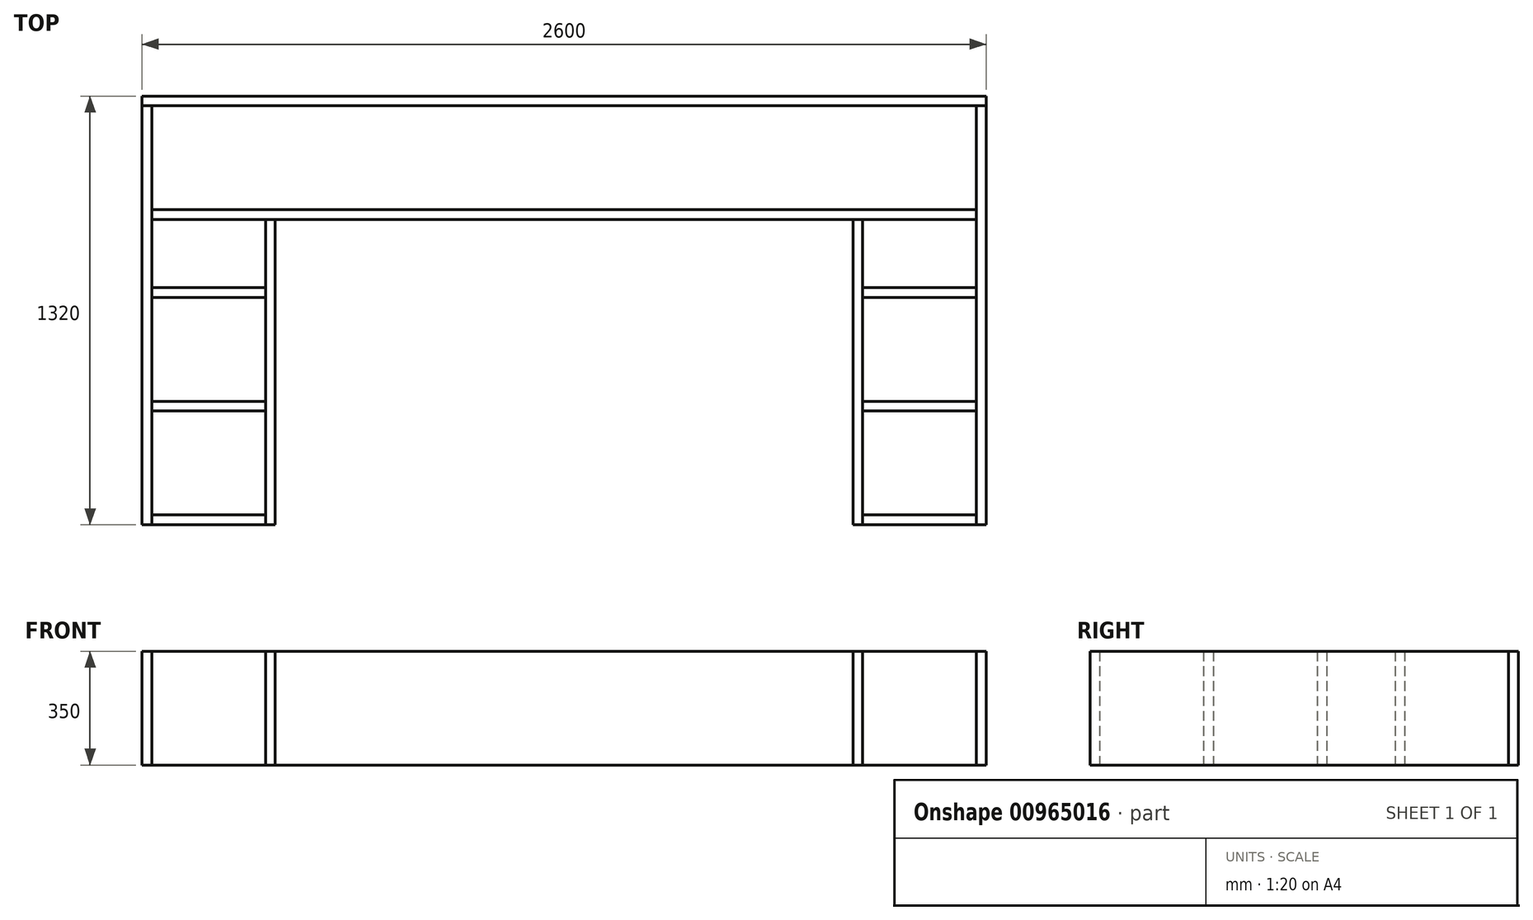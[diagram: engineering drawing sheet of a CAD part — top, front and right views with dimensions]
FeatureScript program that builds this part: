
annotation { "Feature Type Name" : "Feature", "Feature Type Description" : "" }
export const myFeature = defineFeature(function(context is Context, id is Id, definition is map)
    precondition{}
    {
        {
            var Q0;
            Q0=qCreatedBy(makeId("Top.planeOp"),FACE);
            var sketch = newSketch(context, id + "F0", { "sketchPlane" : qUnion([Q0])});
            skLineSegment(sketch, "E0.bottom", {"start": v(1300, 1125) * mm, "end": v(-1300, 1125) * mm});
            skLineSegment(sketch, "E0.top", {"start": v(1300, -1125) * mm, "end": v(-1300, -1125) * mm});
            skLineSegment(sketch, "E0.left", {"start": v(1300, 1125) * mm, "end": v(1300, -1125) * mm});
            skLineSegment(sketch, "E0.right", {"start": v(-1300, 1125) * mm, "end": v(-1300, -1125) * mm});
            skPoint(sketch, "E0.middle", {"position": v(0, 0) * mm});
            skLineSegment(sketch, "E1", {"start": v(-1300, -195) * mm, "end": v(1300, -195) * mm});
            skLineSegment(sketch, "E2", {"start": v(-1300, 1095) * mm, "end": v(1300, 1095) * mm});
            skLineSegment(sketch, "E3", {"start": v(-1270, 1095) * mm, "end": v(-1270, -195) * mm});
            skLineSegment(sketch, "E4", {"start": v(1270, 1095) * mm, "end": v(1270, -195) * mm});
            skLineSegment(sketch, "E5", {"start": v(-1270, 775) * mm, "end": v(1270, 775) * mm});
            skLineSegment(sketch, "E6", {"start": v(-1270, 745) * mm, "end": v(1270, 745) * mm});
            skLineSegment(sketch, "E7", {"start": v(-920, 745) * mm, "end": v(-920, -195) * mm});
            skLineSegment(sketch, "E8", {"start": v(-890, 745) * mm, "end": v(-890, -195) * mm});
            skLineSegment(sketch, "E9", {"start": v(920, 745) * mm, "end": v(920, -195) * mm});
            skLineSegment(sketch, "E10", {"start": v(890, 745) * mm, "end": v(890, -195) * mm});
            skLineSegment(sketch, "E11", {"start": v(-1270, 155) * mm, "end": v(-920, 155) * mm});
            skPoint(sketch, "E11.endSnap0", {"position": v(-920, 275) * mm});
            skLineSegment(sketch, "E12", {"start": v(-1270, 185) * mm, "end": v(-920, 185) * mm});
            skLineSegment(sketch, "E13", {"start": v(-1270, -165) * mm, "end": v(-920, -165) * mm});
            skLineSegment(sketch, "E14", {"start": v(-1270, 505) * mm, "end": v(-920, 505) * mm});
            skLineSegment(sketch, "E15", {"start": v(-1270, 535) * mm, "end": v(-920, 535) * mm});
            skLineSegment(sketch, "E16", {"start": v(920, 155) * mm, "end": v(1270, 155) * mm});
            skLineSegment(sketch, "E17", {"start": v(920, -165) * mm, "end": v(1270, -165) * mm});
            skLineSegment(sketch, "E18", {"start": v(920, 185) * mm, "end": v(1270, 185) * mm});
            skLineSegment(sketch, "E19", {"start": v(920, 505) * mm, "end": v(1270, 505) * mm});
            skLineSegment(sketch, "E20", {"start": v(920, 535) * mm, "end": v(1270, 535) * mm});
            skSolve(sketch);
        }
        {
            var Q0;
            {var subQ5=sQuery(id+"F0.wireOp",EDGE,"E13");Q0=makeQuery(id+"F0.imprint","IMPRINT",FACE,{"disambiguationData":[TD([[makeQuery(id+"F0.imprint","IMPRINT",EDGE,{"derivedFrom":subQ5}),-1.0]])]});}
            var Q1;
            {var subQ0=sQuery(id+"F0.wireOp",EDGE,"E11");Q1=makeQuery(id+"F0.imprint","IMPRINT",FACE,{"disambiguationData":[TD([[makeQuery(id+"F0.imprint","IMPRINT",EDGE,{"derivedFrom":subQ0}),1.0]])]});}
            var Q2;
            {var subQ0=sQuery(id+"F0.wireOp",EDGE,"E14");Q2=makeQuery(id+"F0.imprint","IMPRINT",FACE,{"disambiguationData":[TD([[makeQuery(id+"F0.imprint","IMPRINT",EDGE,{"derivedFrom":subQ0}),1.0]])]});}
            var Q3;
            {var subQ4=sQuery(id+"F0.wireOp",EDGE,"E5");Q3=makeQuery(id+"F0.imprint","IMPRINT",FACE,{"disambiguationData":[TD([[makeQuery(id+"F0.imprint","IMPRINT",EDGE,{"derivedFrom":subQ4}),-1.0]])]});}
            var Q4;
            {var subQ1=sQuery(id+"F0.wireOp",EDGE,"E0.bottom");Q4=makeQuery(id+"F0.imprint","IMPRINT",FACE,{"disambiguationData":[TD([[makeQuery(id+"F0.imprint","IMPRINT",EDGE,{"derivedFrom":subQ1}),1.0]])]});}
            var Q5;
            {var subQ0=sQuery(id+"F0.wireOp",EDGE,"E19");Q5=makeQuery(id+"F0.imprint","IMPRINT",FACE,{"disambiguationData":[TD([[makeQuery(id+"F0.imprint","IMPRINT",EDGE,{"derivedFrom":subQ0}),1.0]])]});}
            var Q6;
            {var subQ0=sQuery(id+"F0.wireOp",EDGE,"E16");Q6=makeQuery(id+"F0.imprint","IMPRINT",FACE,{"disambiguationData":[TD([[makeQuery(id+"F0.imprint","IMPRINT",EDGE,{"derivedFrom":subQ0}),1.0]])]});}
            var Q7;
            {var subQ5=sQuery(id+"F0.wireOp",EDGE,"E17");Q7=makeQuery(id+"F0.imprint","IMPRINT",FACE,{"disambiguationData":[TD([[makeQuery(id+"F0.imprint","IMPRINT",EDGE,{"derivedFrom":subQ5}),-1.0]])]});}
            extrude(context, id + "F1", {"entities" : qUnion([Q0, Q1, Q2, Q3, Q4, Q5, Q6, Q7]), "depth" : 350 * mm, "offsetDistance" : 25 * mm});
        }
        {
            var Q0;
            {var subQ7=sQuery(id+"F0.wireOp",EDGE,"E1");var subQ8=sQuery(id+"F0.wireOp",EDGE,"E0.right");var subQ9=makeQuery(id+"F0.imprint","INTERSECT",VERTEX,{"derivedFrom":[subQ8,subQ7]});Q0=makeQuery(id+"F0.imprint","IMPRINT",FACE,{"disambiguationData":[TD([[makeQuery(id+"F0.imprint","IMPRINT",EDGE,{"disambiguationData":[TD([[subQ9,1.0]])],"derivedFrom":subQ8}),1.0]])]});}
            var Q1;
            {var subQ5=sQuery(id+"F0.wireOp",EDGE,"E8");Q1=makeQuery(id+"F0.imprint","IMPRINT",FACE,{"disambiguationData":[TD([[makeQuery(id+"F0.imprint","IMPRINT",EDGE,{"derivedFrom":subQ5}),-1.0]])]});}
            var Q2;
            {var subQ5=sQuery(id+"F0.wireOp",EDGE,"E10");Q2=makeQuery(id+"F0.imprint","IMPRINT",FACE,{"disambiguationData":[TD([[makeQuery(id+"F0.imprint","IMPRINT",EDGE,{"derivedFrom":subQ5}),1.0]])]});}
            var Q3;
            {var subQ8=sQuery(id+"F0.wireOp",EDGE,"E1");var subQ9=sQuery(id+"F0.wireOp",EDGE,"E0.left");var subQ10=makeQuery(id+"F0.imprint","INTERSECT",VERTEX,{"derivedFrom":[subQ9,subQ8]});Q3=makeQuery(id+"F0.imprint","IMPRINT",FACE,{"disambiguationData":[TD([[makeQuery(id+"F0.imprint","IMPRINT",EDGE,{"disambiguationData":[TD([[subQ10,1.0]])],"derivedFrom":subQ9}),-1.0]])]});}
            extrude(context, id + "F2", {"entities" : qUnion([Q0, Q1, Q2, Q3]), "depth" : 350 * mm, "offsetDistance" : 25 * mm});
        }
    });
